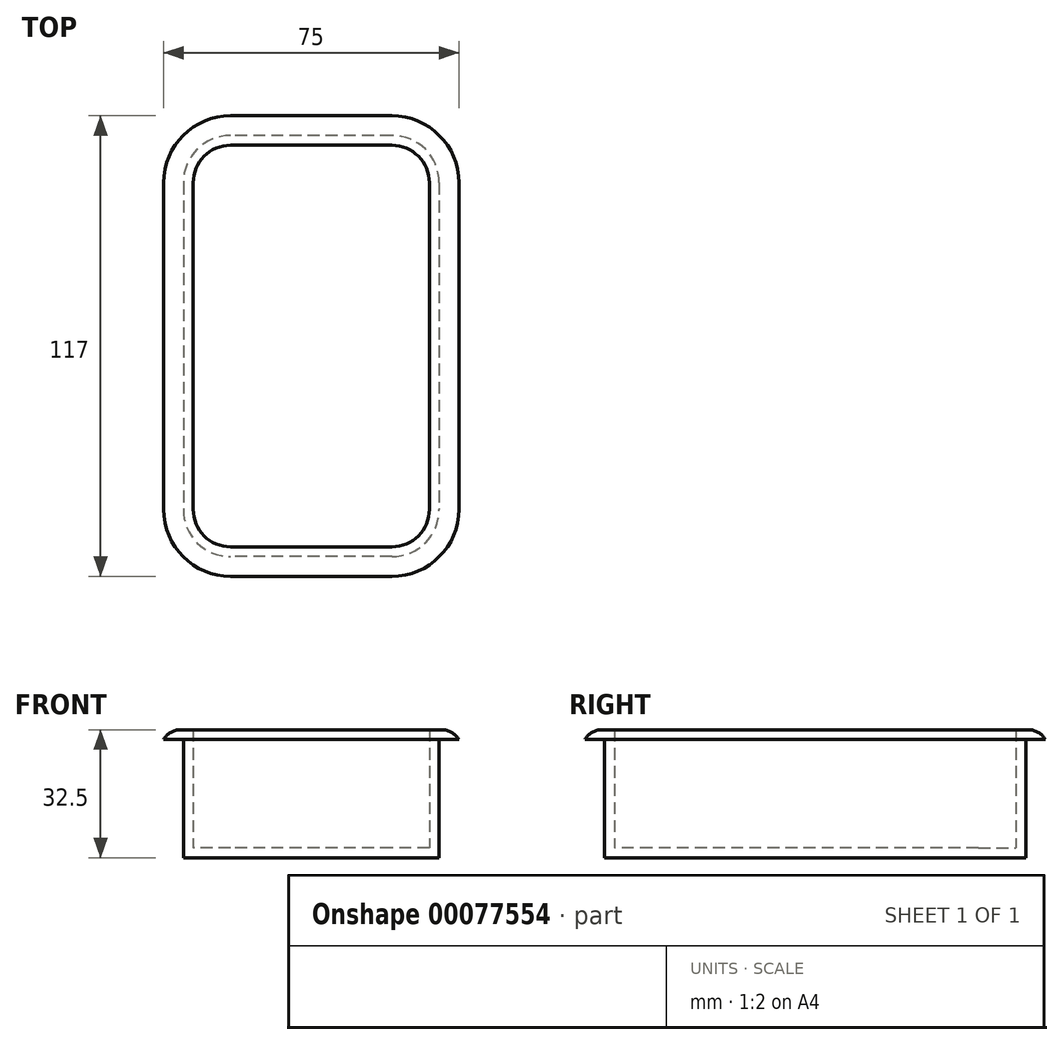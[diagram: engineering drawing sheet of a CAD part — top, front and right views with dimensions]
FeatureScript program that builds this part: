
annotation { "Feature Type Name" : "Feature", "Feature Type Description" : "" }
export const myFeature = defineFeature(function(context is Context, id is Id, definition is map)
    precondition{}
    {
        {
            var Q0;
            Q0=qCreatedBy(makeId("Top.planeOp"),FACE);
            var sketch = newSketch(context, id + "F0", { "sketchPlane" : qUnion([Q0])});
            skLineSegment(sketch, "E0.bottom", {"start": v(20.5, 53.5) * mm, "end": v(-20.5, 53.5) * mm});
            skLineSegment(sketch, "E0.top", {"start": v(20.5, -53.5) * mm, "end": v(-20.5, -53.5) * mm});
            skLineSegment(sketch, "E0.left", {"start": v(32.5, 41.5) * mm, "end": v(32.5, -41.5) * mm});
            skLineSegment(sketch, "E0.right", {"start": v(-32.5, 41.5) * mm, "end": v(-32.5, -41.5) * mm});
            skPoint(sketch, "E0.middle", {"position": v(0, 0) * mm});
            skPoint(sketch, "E1.visualSharp", {"position": v(-32.5, 53.5) * mm});
            skArc(sketch, "E1.filletArc", {"start": v(-20.5, 53.5) * mm, "mid": v(-28.99, 49.99) * mm, "end": v(-32.5, 41.5) * mm});
            skPoint(sketch, "E2.visualSharp", {"position": v(32.5, 53.5) * mm});
            skArc(sketch, "E2.filletArc", {"start": v(32.5, 41.5) * mm, "mid": v(28.99, 49.99) * mm, "end": v(20.5, 53.5) * mm});
            skPoint(sketch, "E3.visualSharp", {"position": v(32.5, -53.5) * mm});
            skArc(sketch, "E3.filletArc", {"start": v(20.5, -53.5) * mm, "mid": v(28.99, -49.99) * mm, "end": v(32.5, -41.5) * mm});
            skPoint(sketch, "E4.visualSharp", {"position": v(-32.5, -53.5) * mm});
            skArc(sketch, "E4.filletArc", {"start": v(-32.5, -41.5) * mm, "mid": v(-28.99, -49.99) * mm, "end": v(-20.5, -53.5) * mm});
            skSolve(sketch);
        }
        {
            var Q0;
            Q0=makeQuery(id+"F0.imprint","IMPRINT",FACE,{"disambiguationData":[TD([[makeQuery(id+"F0.imprint","IMPRINT",EDGE,{"derivedFrom":sQuery(id+"F0.wireOp",EDGE,"E0.bottom")}),1.0]])]});
            extrude(context, id + "F1", {"entities" : qUnion([Q0]), "depth" : 30 * mm});
        }
        {
            var Q0;
            Q0=makeQuery(id+"F1.opExtrude","CAP_FACE",FACE,{"disambiguationData":[OSD([sQuery(id+"F0.wireOp",EDGE,"E0.bottom"),sQuery(id+"F0.wireOp",EDGE,"E0.top"),sQuery(id+"F0.wireOp",EDGE,"E0.left"),sQuery(id+"F0.wireOp",EDGE,"E0.right"),sQuery(id+"F0.wireOp",EDGE,"E1.filletArc"),sQuery(id+"F0.wireOp",EDGE,"E2.filletArc"),sQuery(id+"F0.wireOp",EDGE,"E3.filletArc"),sQuery(id+"F0.wireOp",EDGE,"E4.filletArc")])],"isStart":false});
            shell(context, id + "F2", {"entities" : qUnion([Q0]), "thickness" : 2.5 * mm});
        }
        {
            var Q0;
            Q0=makeQuery(id+"F1.opExtrude","CAP_FACE",FACE,{"disambiguationData":[OSD([sQuery(id+"F0.wireOp",EDGE,"E0.bottom"),sQuery(id+"F0.wireOp",EDGE,"E0.top"),sQuery(id+"F0.wireOp",EDGE,"E0.left"),sQuery(id+"F0.wireOp",EDGE,"E0.right"),sQuery(id+"F0.wireOp",EDGE,"E1.filletArc"),sQuery(id+"F0.wireOp",EDGE,"E2.filletArc"),sQuery(id+"F0.wireOp",EDGE,"E3.filletArc"),sQuery(id+"F0.wireOp",EDGE,"E4.filletArc")])],"isStart":false});
            var sketch = newSketch(context, id + "F3", { "sketchPlane" : qUnion([Q0])});
            skLineSegment(sketch, "E5.bottom", {"start": v(20.5, -58.5) * mm, "end": v(-20.5, -58.5) * mm});
            skLineSegment(sketch, "E5.top", {"start": v(20.5, 58.5) * mm, "end": v(-20.5, 58.5) * mm});
            skLineSegment(sketch, "E5.left", {"start": v(37.5, -41.5) * mm, "end": v(37.5, 41.5) * mm});
            skLineSegment(sketch, "E5.right", {"start": v(-37.5, -41.5) * mm, "end": v(-37.5, 41.5) * mm});
            skPoint(sketch, "E5.middle", {"position": v(0, 0) * mm});
            skPoint(sketch, "E6.visualSharp", {"position": v(-37.5, 58.5) * mm});
            skArc(sketch, "E6.filletArc", {"start": v(-20.5, 58.5) * mm, "mid": v(-32.52, 53.52) * mm, "end": v(-37.5, 41.5) * mm});
            skPoint(sketch, "E7.visualSharp", {"position": v(37.5, 58.5) * mm});
            skArc(sketch, "E7.filletArc", {"start": v(37.5, 41.5) * mm, "mid": v(32.52, 53.52) * mm, "end": v(20.5, 58.5) * mm});
            skPoint(sketch, "E8.visualSharp", {"position": v(37.5, -58.5) * mm});
            skArc(sketch, "E8.filletArc", {"start": v(20.5, -58.5) * mm, "mid": v(32.52, -53.52) * mm, "end": v(37.5, -41.5) * mm});
            skPoint(sketch, "E9.visualSharp", {"position": v(-37.5, -58.5) * mm});
            skArc(sketch, "E9.filletArc", {"start": v(-37.5, -41.5) * mm, "mid": v(-32.52, -53.52) * mm, "end": v(-20.5, -58.5) * mm});
            skSolve(sketch);
        }
        {
            var Q0;
            {var subQ0=sQuery(id+"F0.wireOp",EDGE,"E0.bottom");var subQ1=makeQuery(id+"F1.opExtrude","CAP_EDGE",EDGE,{"disambiguationData":[OSD([subQ0])],"isStart":false});Q0=makeQuery(id+"F3.imprint","IMPRINT",FACE,{"disambiguationData":[TD([[makeQuery(id+"F3.imprint","IMPRINT",EDGE,{"derivedFrom":subQ1}),1.0]])]});}
            var Q1;
            Q1=makeQuery(id+"F3.imprint","IMPRINT",FACE,{"disambiguationData":[TD([[makeQuery(id+"F3.imprint","IMPRINT",EDGE,{"derivedFrom":sQuery(id+"F3.wireOp",EDGE,"E5.bottom")}),-1.0]])]});
            extrude(context, id + "F4", {"entities" : qUnion([Q0, Q1]), "operationType" : NewBodyOperationType.ADD, "depth" : 2.5 * mm});
        }
        {
            var Q0;
            Q0=makeQuery(id+"F4.opExtrude","CAP_EDGE",EDGE,{"disambiguationData":[OSD([sQuery(id+"F3.wireOp",EDGE,"E5.left")])],"isStart":false});
            fillet(context, id + "F5", {"entities" : qUnion([Q0]), "radius" : 5 * mm, "tangentPropagation" : true, "allowEdgeOverflow" : false});
        }
    });
